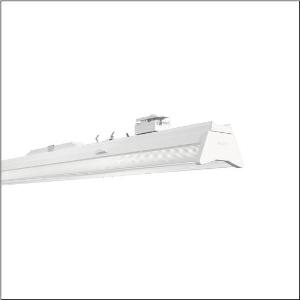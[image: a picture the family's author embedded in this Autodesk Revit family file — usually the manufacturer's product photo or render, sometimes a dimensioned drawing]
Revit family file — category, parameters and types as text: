
# Revit family: licross_r__21_performance_mo_52td16cn49xg_b518
name_source: partatom
category: Lighting Fixtures
units: mm (PartAtom-declared; Revit-internal decimal feet)

## family parameters
Cut with Voids When Loaded = No
Host = Face
Light Source = No
Part Type = Normal
Room Calculation Point = No
Round Connector Dimension = Use Diameter
Shared = No

## types (1)
- --- (1 x LED, 9240 lm, 50.4 W, 4000K)
    Apparent Load = 50 VA
    CIE Flux Codes = 66 88 96 79 100
    Color Rendering = 80
    Color Temperature = 4000K
    Default Elevation = 1800 mm
    Description = Licross® 21 Performance MO, luminaire insert, of sheet steel, galvanised, coil coated, white, length: 1.500mm, width: 120mm, height: 123mm, LED rated luminous flux: 9.240lm, light colour: 840, SDCM (Standard Deviation of Colour Matching)MacAdam ≤ 3 SDCM (initial), control gear: ON/OFF Multilumen, CLOi, with plug, 3-pole, with phase selection, mains connection: 220..240V, AC, 50/60Hz, start of lifetime: 50W, end of service life: 61W, internal wiring halogen-free, primary light control with lens, of plastic, primary optical cover: cover, of PMMA, light emission: direct/indirect distribution, primary light characteristic: symmetric, protection rating (complete): IP54, insulation class (complete): insulation class I (protective earthing), certification: CE, ENEC, UKCA, protection symbol: D if used in an environment with non-conductive dust loads with corresponding accessories, impact resistance: IK06, permissible ambient temperature for indoor applications: -35..+45°C, corresponds to IFS (International Featured Standards) requirements for safety and quality in the food industry, reducing of maximum allowable ambient temperature of 5°C with ceiling mounting, LABS conformity tested according to VDMA 24364:2018-05, packaging unit: 1 piece
    Height = 114 mm
    Lamp = 1 x LED
    Lamp Light Flux = 9240 lm
    Lamp Power = 50.4 W
    Lamp count = 1
    Length = 1500 mm
    Luminous efficacy = 183 lm/W
    Manufacturer = Siteco
    ModVariant = No
    Model = 52TD16CN49XG
    Mounting Place = Ceiling
    Mounting Type = Pendant
    Number of Poles = 1
    OnlyDefault = Yes
    Power Factor = 1
    Product Name = Licross® 21 Performance MO
    Product group = luminaire insert | ceiling pendant
    ProductGroupID = 901
    Protection Class = Protection class I
    Protection Degree = IP 54
    RLX_Detail_Level = 1
    RLX_Emergency_Light_Flux = 0 lm
    RLX_Emergency_Type = 0
    RLX_Emergency_Type_DB = No
    RlxData = <blob elided: 31921 chars, md5=a369bd1b>
    Socket = socket
    Standby Power = 0 W
    System Light Flux = 9240 lm
    System Power = 50 W
    Type Comments = factory setting: luminous flux: 100 % | (A | C | E) | 117 mA
    Type Image = l_1256138.jpg
    URL = http://relux.com
    VarID = @adj_115471
    Voltage = 0 V
    Weight = 0.00 kg
    Width = 120 mm

## geometry (parser evidence)
native form markers: Blend x4, Sweep x11
no freeform markers — native parametric forms only
